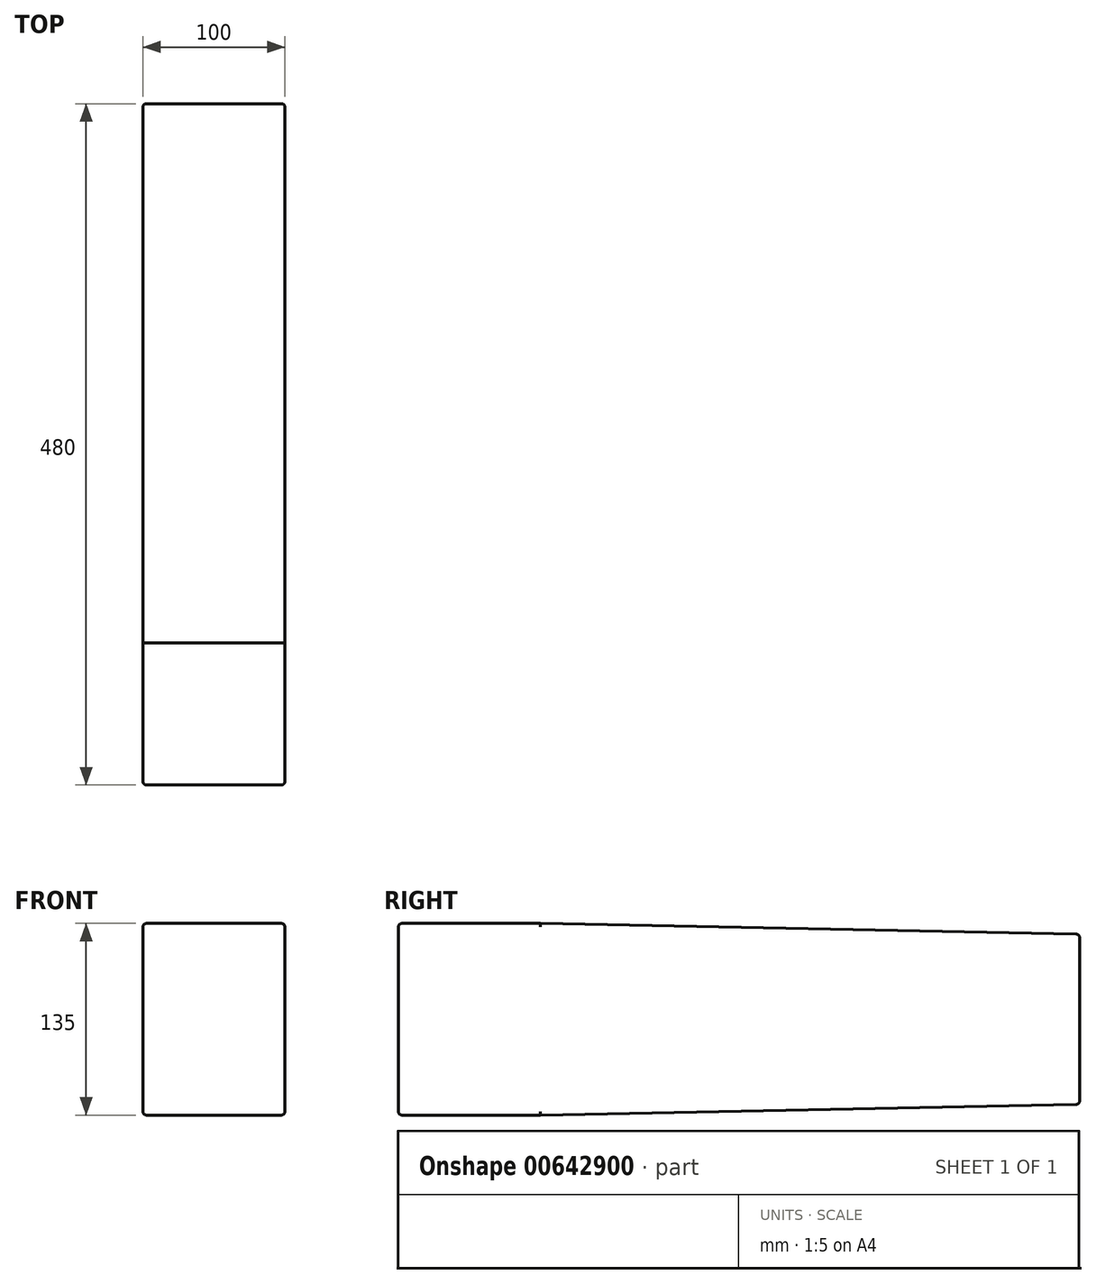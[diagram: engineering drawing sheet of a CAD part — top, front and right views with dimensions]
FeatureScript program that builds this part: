
annotation { "Feature Type Name" : "Feature", "Feature Type Description" : "" }
export const myFeature = defineFeature(function(context is Context, id is Id, definition is map)
    precondition{}
    {
        {
            var Q0;
            Q0=qCreatedBy(makeId("Right.planeOp"),FACE);
            var sketch = newSketch(context, id + "F0", { "sketchPlane" : qUnion([Q0])});
            skLineSegment(sketch, "E0.bottom", {"start": v(50, 67.5) * mm, "end": v(-50, 67.5) * mm});
            skLineSegment(sketch, "E0.top", {"start": v(50, -67.5) * mm, "end": v(-50, -67.5) * mm});
            skLineSegment(sketch, "E0.left", {"start": v(50, 67.5) * mm, "end": v(50, -67.5) * mm});
            skLineSegment(sketch, "E0.right", {"start": v(-50, 67.5) * mm, "end": v(-50, -67.5) * mm});
            skPoint(sketch, "E0.middle", {"position": v(0, 0) * mm});
            skLineSegment(sketch, "E1.bottom", {"start": v(370, -60) * mm, "end": v(430, -60) * mm});
            skLineSegment(sketch, "E1.top", {"start": v(370, 60) * mm, "end": v(430, 60) * mm});
            skLineSegment(sketch, "E1.left", {"start": v(370, -60) * mm, "end": v(370, 60) * mm});
            skLineSegment(sketch, "E1.right", {"start": v(430, -60) * mm, "end": v(430, 60) * mm});
            skPoint(sketch, "E1.middle", {"position": v(400, 0) * mm});
            skLineSegment(sketch, "E2", {"start": v(50, 67.5) * mm, "end": v(430, 60) * mm});
            skLineSegment(sketch, "E3", {"start": v(50, -67.5) * mm, "end": v(430, -60) * mm});
            skSolve(sketch);
        }
        {
            var Q0;
            Q0=qSketchRegion(id+"F0",true);
            extrude(context, id + "F1", {"entities" : qUnion([Q0]), "depth" : 100 * mm, "offsetDistance" : 25 * mm});
        }
        {
            var Q0;
            Q0=makeQuery(id+"F1.opExtrude","CAP_EDGE",EDGE,{"disambiguationData":[OSD([sQuery(id+"F0.wireOp",EDGE,"E2")])],"isStart":false});
            var Q1;
            Q1=makeQuery(id+"F1.opExtrude","CAP_EDGE",EDGE,{"disambiguationData":[OSD([sQuery(id+"F0.wireOp",EDGE,"E1.right")])],"isStart":false});
            var Q2;
            Q2=makeQuery(id+"F1.opExtrude","CAP_EDGE",EDGE,{"disambiguationData":[OSD([sQuery(id+"F0.wireOp",EDGE,"E3")])],"isStart":false});
            var Q3;
            Q3=makeQuery(id+"F1.opExtrude","CAP_EDGE",EDGE,{"disambiguationData":[OSD([sQuery(id+"F0.wireOp",EDGE,"E0.bottom")])],"isStart":false});
            var Q4;
            Q4=makeQuery(id+"F1.opExtrude","CAP_EDGE",EDGE,{"disambiguationData":[OSD([sQuery(id+"F0.wireOp",EDGE,"E0.right")])],"isStart":false});
            var Q5;
            Q5=makeQuery(id+"F1.opExtrude","CAP_EDGE",EDGE,{"disambiguationData":[OSD([sQuery(id+"F0.wireOp",EDGE,"E0.top")])],"isStart":false});
            var Q6;
            Q6=makeQuery(id+"F1.opExtrude","SWEPT_EDGE",EDGE,{"disambiguationData":[OSD([sQuery(id+"F0.wireOp",EDGE,"E0.top"),sQuery(id+"F0.wireOp",EDGE,"E0.right")])]});
            var Q7;
            Q7=makeQuery(id+"F1.opExtrude","CAP_EDGE",EDGE,{"disambiguationData":[OSD([sQuery(id+"F0.wireOp",EDGE,"E0.right")])],"isStart":true});
            var Q8;
            Q8=makeQuery(id+"F1.opExtrude","CAP_EDGE",EDGE,{"disambiguationData":[OSD([sQuery(id+"F0.wireOp",EDGE,"E0.bottom")])],"isStart":true});
            var Q9;
            Q9=makeQuery(id+"F1.opExtrude","CAP_EDGE",EDGE,{"disambiguationData":[OSD([sQuery(id+"F0.wireOp",EDGE,"E3")])],"isStart":true});
            var Q10;
            Q10=makeQuery(id+"F1.opExtrude","CAP_EDGE",EDGE,{"disambiguationData":[OSD([sQuery(id+"F0.wireOp",EDGE,"E0.top")])],"isStart":true});
            var Q11;
            Q11=makeQuery(id+"F1.opExtrude","SWEPT_EDGE",EDGE,{"disambiguationData":[OSD([sQuery(id+"F0.wireOp",EDGE,"E1.bottom"),sQuery(id+"F0.wireOp",EDGE,"E1.right"),sQuery(id+"F0.wireOp",EDGE,"E3")])]});
            var Q12;
            Q12=makeQuery(id+"F1.opExtrude","CAP_EDGE",EDGE,{"disambiguationData":[OSD([sQuery(id+"F0.wireOp",EDGE,"E1.right")])],"isStart":true});
            var Q13;
            Q13=makeQuery(id+"F1.opExtrude","SWEPT_EDGE",EDGE,{"disambiguationData":[OSD([sQuery(id+"F0.wireOp",EDGE,"E1.top"),sQuery(id+"F0.wireOp",EDGE,"E1.right"),sQuery(id+"F0.wireOp",EDGE,"E2")])]});
            var Q14;
            Q14=makeQuery(id+"F1.opExtrude","CAP_EDGE",EDGE,{"disambiguationData":[OSD([sQuery(id+"F0.wireOp",EDGE,"E2")])],"isStart":true});
            var Q15;
            Q15=makeQuery(id+"F1.opExtrude","SWEPT_EDGE",EDGE,{"disambiguationData":[OSD([sQuery(id+"F0.wireOp",EDGE,"E0.bottom"),sQuery(id+"F0.wireOp",EDGE,"E0.right")])]});
            fillet(context, id + "F2", {"entities" : qUnion([Q0, Q1, Q2, Q3, Q4, Q5, Q6, Q7, Q8, Q9, Q10, Q11, Q12, Q13, Q14, Q15]), "radius" : 2.5 * mm, "tangentPropagation" : true, "allowEdgeOverflow" : false});
        }
    });
